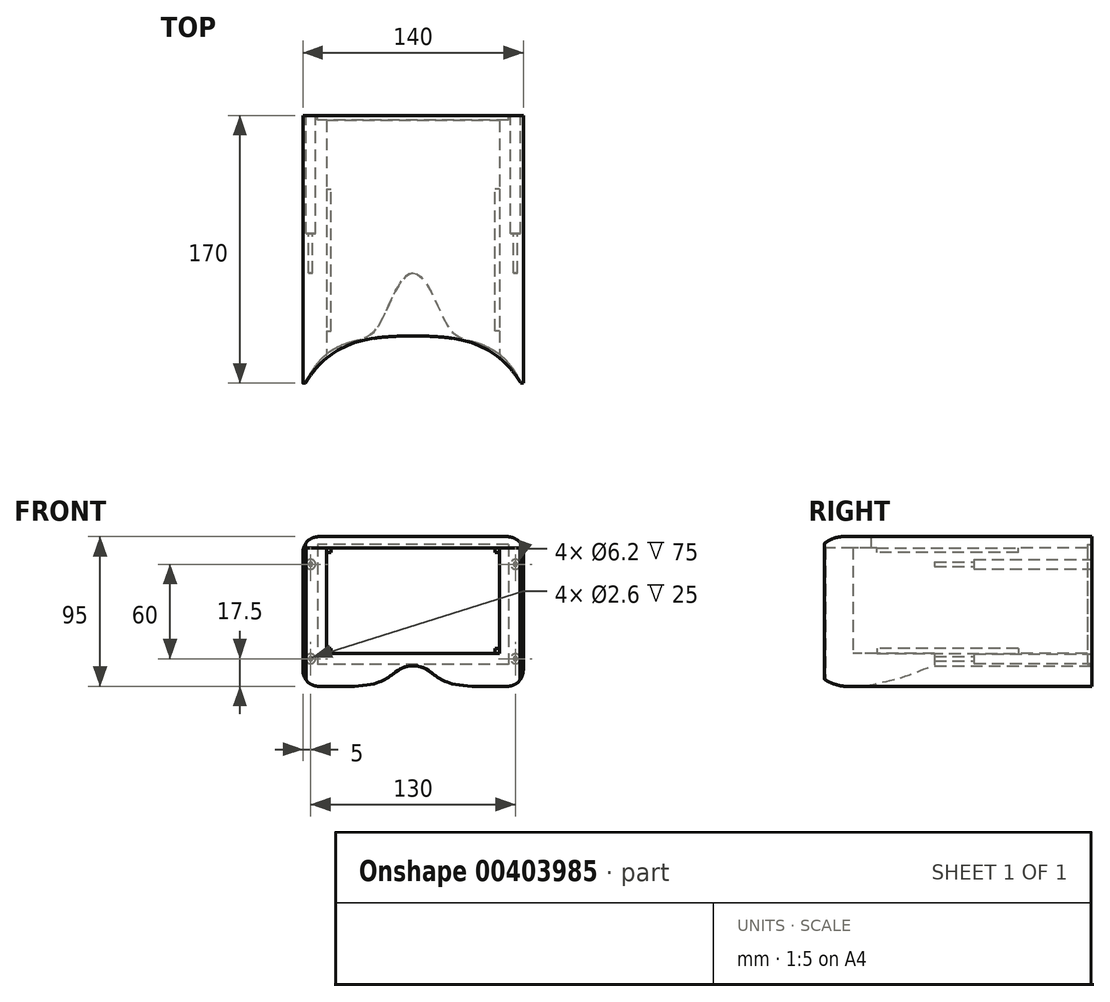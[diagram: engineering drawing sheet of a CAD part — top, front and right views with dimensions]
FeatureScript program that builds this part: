
annotation { "Feature Type Name" : "Feature", "Feature Type Description" : "" }
export const myFeature = defineFeature(function(context is Context, id is Id, definition is map)
    precondition{}
    {
        {
            var Q0;
            Q0=qCreatedBy(makeId("Top.planeOp"),FACE);
            var sketch = newSketch(context, id + "F0", { "sketchPlane" : qUnion([Q0])});
            skLineSegment(sketch, "E0.bottom", {"start": v(70, 85) * mm, "end": v(-70, 85) * mm});
            skLineSegment(sketch, "E0.top", {"start": v(70, -85) * mm, "end": v(-70, -85) * mm});
            skLineSegment(sketch, "E0.left", {"start": v(70, 85) * mm, "end": v(70, -85) * mm});
            skLineSegment(sketch, "E0.right", {"start": v(-70, 85) * mm, "end": v(-70, -85) * mm});
            skPoint(sketch, "E0.middle", {"position": v(0, 0) * mm});
            skSolve(sketch);
        }
        {
            var Q0;
            Q0=qSketchRegion(id+"F0",true);
            extrude(context, id + "F1", {"entities" : qUnion([Q0]), "depth" : 95 * mm});
        }
        {
            var Q0;
            Q0=makeQuery(id+"F1.opExtrude","SWEPT_FACE",FACE,{"disambiguationData":[OSD([sQuery(id+"F0.wireOp",EDGE,"E0.top")])]});
            var sketch = newSketch(context, id + "F2", { "sketchPlane" : qUnion([Q0])});
            skLineSegment(sketch, "E1.bottom", {"start": v(-55, 88) * mm, "end": v(55, 88) * mm});
            skLineSegment(sketch, "E1.top", {"start": v(-55, 21) * mm, "end": v(55, 21) * mm});
            skLineSegment(sketch, "E1.left", {"start": v(-55, 88) * mm, "end": v(-55, 21) * mm});
            skLineSegment(sketch, "E1.right", {"start": v(55, 88) * mm, "end": v(55, 21) * mm});
            skSolve(sketch);
        }
        {
            var Q0;
            Q0=qSketchRegion(id+"F2",true);
            extrude(context, id + "F3", {"entities" : qUnion([Q0]), "operationType" : NewBodyOperationType.REMOVE, "endBound" : BoundingType.THROUGH_ALL, "oppositeDirection" : true, "depth" : 25 * mm});
        }
        {
            var Q0;
            Q0=makeQuery(id+"F1.opExtrude","CAP_FACE",FACE,{"disambiguationData":[OSD([sQuery(id+"F0.wireOp",EDGE,"E0.bottom"),sQuery(id+"F0.wireOp",EDGE,"E0.top"),sQuery(id+"F0.wireOp",EDGE,"E0.left"),sQuery(id+"F0.wireOp",EDGE,"E0.right")])],"isStart":true});
            var sketch = newSketch(context, id + "F4", { "sketchPlane" : qUnion([Q0])});
            skLineSegment(sketch, "E2", {"start": v(0, -85) * mm, "end": v(0, 85) * mm, "construction": true});
            skLineSegment(sketch, "E3.1.0.0", {"start": v(-10, -85) * mm, "end": v(-10, 85) * mm, "construction": true});
            skLineSegment(sketch, "E3.2.0.0", {"start": v(-20, -85) * mm, "end": v(-20, 85) * mm, "construction": true});
            skLineSegment(sketch, "E3.3.0.0", {"start": v(-30, -85) * mm, "end": v(-30, 85) * mm, "construction": true});
            skLineSegment(sketch, "E3.4.0.0", {"start": v(-40, -85) * mm, "end": v(-40, 85) * mm, "construction": true});
            skLineSegment(sketch, "E3.5.0.0", {"start": v(-50, -85) * mm, "end": v(-50, 85) * mm, "construction": true});
            skLineSegment(sketch, "E3.6.0.0", {"start": v(-60, -85) * mm, "end": v(-60, 85) * mm, "construction": true});
            skLineSegment(sketch, "E3.direction1", {"start": v(0, -85) * mm, "end": v(-10, -85) * mm, "construction": true});
            skLineSegment(sketch, "E4.1.0.0", {"start": v(10, -85) * mm, "end": v(10, 85) * mm, "construction": true});
            skLineSegment(sketch, "E4.2.0.0", {"start": v(20, -85) * mm, "end": v(20, 85) * mm, "construction": true});
            skLineSegment(sketch, "E4.3.0.0", {"start": v(30, -85) * mm, "end": v(30, 85) * mm, "construction": true});
            skLineSegment(sketch, "E4.4.0.0", {"start": v(40, -85) * mm, "end": v(40, 85) * mm, "construction": true});
            skLineSegment(sketch, "E4.5.0.0", {"start": v(50, -85) * mm, "end": v(50, 85) * mm, "construction": true});
            skLineSegment(sketch, "E4.6.0.0", {"start": v(60, -85) * mm, "end": v(60, 85) * mm, "construction": true});
            skLineSegment(sketch, "E4.direction1", {"start": v(0, -85) * mm, "end": v(10, -85) * mm, "construction": true});
            skLineSegment(sketch, "E5", {"start": v(70, 15) * mm, "end": v(-70, 15) * mm, "construction": true});
            skLineSegment(sketch, "E6.0.1.0", {"start": v(70, 25) * mm, "end": v(-70, 25) * mm, "construction": true});
            skLineSegment(sketch, "E6.0.2.0", {"start": v(70, 35) * mm, "end": v(-70, 35) * mm, "construction": true});
            skLineSegment(sketch, "E6.0.3.0", {"start": v(70, 45) * mm, "end": v(-70, 45) * mm, "construction": true});
            skLineSegment(sketch, "E6.0.4.0", {"start": v(70, 55) * mm, "end": v(-70, 55) * mm, "construction": true});
            skLineSegment(sketch, "E6.0.5.0", {"start": v(70, 65) * mm, "end": v(-70, 65) * mm, "construction": true});
            skLineSegment(sketch, "E6.0.6.0", {"start": v(70, 75) * mm, "end": v(-70, 75) * mm, "construction": true});
            skLineSegment(sketch, "E6.1.0.0", {"start": v(95, 15) * mm, "end": v(-45, 15) * mm, "construction": true});
            skLineSegment(sketch, "E6.1.1.0", {"start": v(95, 25) * mm, "end": v(-45, 25) * mm, "construction": true});
            skLineSegment(sketch, "E6.1.2.0", {"start": v(95, 35) * mm, "end": v(-45, 35) * mm, "construction": true});
            skLineSegment(sketch, "E6.1.3.0", {"start": v(95, 45) * mm, "end": v(-45, 45) * mm, "construction": true});
            skLineSegment(sketch, "E6.1.4.0", {"start": v(95, 55) * mm, "end": v(-45, 55) * mm, "construction": true});
            skLineSegment(sketch, "E6.1.5.0", {"start": v(95, 65) * mm, "end": v(-45, 65) * mm, "construction": true});
            skLineSegment(sketch, "E6.1.6.0", {"start": v(95, 75) * mm, "end": v(-45, 75) * mm, "construction": true});
            skLineSegment(sketch, "E6.2.0.0", {"start": v(120, 15) * mm, "end": v(-20, 15) * mm, "construction": true});
            skLineSegment(sketch, "E6.2.1.0", {"start": v(120, 25) * mm, "end": v(-20, 25) * mm, "construction": true});
            skLineSegment(sketch, "E6.2.2.0", {"start": v(120, 35) * mm, "end": v(-20, 35) * mm, "construction": true});
            skLineSegment(sketch, "E6.2.3.0", {"start": v(120, 45) * mm, "end": v(-20, 45) * mm, "construction": true});
            skLineSegment(sketch, "E6.2.4.0", {"start": v(120, 55) * mm, "end": v(-20, 55) * mm, "construction": true});
            skLineSegment(sketch, "E6.2.5.0", {"start": v(120, 65) * mm, "end": v(-20, 65) * mm, "construction": true});
            skLineSegment(sketch, "E6.2.6.0", {"start": v(120, 75) * mm, "end": v(-20, 75) * mm, "construction": true});
            skLineSegment(sketch, "E6.direction1", {"start": v(-70, 15) * mm, "end": v(-45, 15) * mm, "construction": true});
            skLineSegment(sketch, "E6.direction2", {"start": v(-70, 15) * mm, "end": v(-70, 25) * mm, "construction": true});
            skFitSpline(sketch, "E7", {"points": [v(0, 15) * mm, v(20, 45) * mm, v(31.85, 56.6) * mm, v(68.26, 85) * mm], "startDerivative": vector(65.7, 0) * mm, "endDerivative": vector(77.5, 177.86) * mm});
            skFitSpline(sketch, "E8.MirrorCS", {"points": [v(0, 15) * mm, v(-20, 45) * mm, v(-31.85, 56.6) * mm, v(-68.26, 85) * mm], "startDerivative": vector(-65.7, 0) * mm, "endDerivative": vector(-77.5, 177.86) * mm});
            skLineSegment(sketch, "E9", {"start": v(68.26, 85) * mm, "end": v(-68.26, 85) * mm});
            skSolve(sketch);
        }
        {
            var Q0;
            Q0=makeQuery(id+"F4.imprint","IMPRINT",FACE,{"disambiguationData":[TD([[makeQuery(id+"F4.imprint","IMPRINT",EDGE,{"derivedFrom":sQuery(id+"F4.wireOp",EDGE,"E7")}),1.0]])]});
            extrude(context, id + "F5", {"entities" : qUnion([Q0]), "operationType" : NewBodyOperationType.REMOVE, "oppositeDirection" : true, "depth" : 88 * mm});
        }
        {
            var Q0;
            Q0=makeQuery(id+"F1.opExtrude","CAP_FACE",FACE,{"disambiguationData":[OSD([sQuery(id+"F0.wireOp",EDGE,"E0.bottom"),sQuery(id+"F0.wireOp",EDGE,"E0.top"),sQuery(id+"F0.wireOp",EDGE,"E0.left"),sQuery(id+"F0.wireOp",EDGE,"E0.right")])],"isStart":false});
            var sketch = newSketch(context, id + "F6", { "sketchPlane" : qUnion([Q0])});
            skLineSegment(sketch, "E10", {"start": v(-70, -55) * mm, "end": v(70, -55) * mm, "construction": true});
            skLineSegment(sketch, "E11", {"start": v(68.3, -85) * mm, "end": v(68.3, -55) * mm, "construction": true});
            skLineSegment(sketch, "E12", {"start": v(-68.36, -85) * mm, "end": v(-68.36, -55) * mm, "construction": true});
            skLineSegment(sketch, "E13", {"start": v(0, -85) * mm, "end": v(0, -55) * mm, "construction": true});
            skFitSpline(sketch, "E14", {"points": [v(0, -55) * mm, v(-47.97, -64.27) * mm, v(-68.36, -85) * mm], "startDerivative": vector(-134.93, 0) * mm, "endDerivative": vector(-37.97, -66.04) * mm});
            skFitSpline(sketch, "E15.MirrorCS", {"points": [v(0, -55) * mm, v(47.97, -64.27) * mm, v(68.36, -85) * mm], "startDerivative": vector(134.93, 0) * mm, "endDerivative": vector(37.97, -66.04) * mm});
            skLineSegment(sketch, "E16", {"start": v(-68.36, -85) * mm, "end": v(68.36, -85) * mm});
            skSolve(sketch);
        }
        {
            var Q0;
            Q0=makeQuery(id+"F6.imprint","IMPRINT",FACE,{"disambiguationData":[TD([[makeQuery(id+"F6.imprint","IMPRINT",EDGE,{"derivedFrom":sQuery(id+"F6.wireOp",EDGE,"E14")}),1.0]])]});
            extrude(context, id + "F7", {"entities" : qUnion([Q0]), "operationType" : NewBodyOperationType.REMOVE, "endBound" : BoundingType.UP_TO_NEXT, "oppositeDirection" : true, "depth" : 25 * mm});
        }
        {
            var Q0;
            Q0=makeQuery(id+"F1.opExtrude","CAP_EDGE",EDGE,{"disambiguationData":[OSD([sQuery(id+"F0.wireOp",EDGE,"E0.left")])],"isStart":false});
            var Q1;
            Q1=makeQuery(id+"F1.opExtrude","CAP_EDGE",EDGE,{"disambiguationData":[OSD([sQuery(id+"F0.wireOp",EDGE,"E0.left")])],"isStart":true});
            var Q2;
            Q2=makeQuery(id+"F1.opExtrude","CAP_EDGE",EDGE,{"disambiguationData":[OSD([sQuery(id+"F0.wireOp",EDGE,"E0.right")])],"isStart":true});
            var Q3;
            Q3=makeQuery(id+"F1.opExtrude","CAP_EDGE",EDGE,{"disambiguationData":[OSD([sQuery(id+"F0.wireOp",EDGE,"E0.right")])],"isStart":false});
            fillet(context, id + "F8", {"entities" : qUnion([Q0, Q1, Q2, Q3]), "radius" : 10 * mm, "tangentPropagation" : true, "allowEdgeOverflow" : false});
        }
        {
            var Q0;
            Q0=makeQuery(id+"F1.opExtrude","SWEPT_FACE",FACE,{"disambiguationData":[OSD([sQuery(id+"F0.wireOp",EDGE,"E0.bottom")])]});
            var sketch = newSketch(context, id + "F9", { "sketchPlane" : qUnion([Q0])});
            skLineSegment(sketch, "E17", {"start": v(0, 21) * mm, "end": v(0, 0) * mm, "construction": true});
            skLineSegment(sketch, "E18", {"start": v(-70, 13) * mm, "end": v(70, 13) * mm, "construction": true});
            skLineSegment(sketch, "E19", {"start": v(-40, 21) * mm, "end": v(-40, 0) * mm, "construction": true});
            skFitSpline(sketch, "E20", {"points": [v(0, 13) * mm, v(-40, 0) * mm], "startDerivative": vector(-42.54, 0) * mm, "endDerivative": vector(-86.95, 0) * mm});
            skFitSpline(sketch, "E21.MirrorCS", {"points": [v(0, 13) * mm, v(40, 0) * mm], "startDerivative": vector(42.54, 0) * mm, "endDerivative": vector(86.95, 0) * mm});
            skLineSegment(sketch, "E22", {"start": v(40, 0) * mm, "end": v(-40, 0) * mm});
            skSolve(sketch);
        }
        {
            var Q0;
            Q0=makeQuery(id+"F9.imprint","IMPRINT",FACE,{"disambiguationData":[TD([[makeQuery(id+"F9.imprint","IMPRINT",EDGE,{"derivedFrom":sQuery(id+"F9.wireOp",EDGE,"E20")}),1.0]])]});
            extrude(context, id + "F10", {"entities" : qUnion([Q0]), "operationType" : NewBodyOperationType.REMOVE, "endBound" : BoundingType.THROUGH_ALL, "oppositeDirection" : true, "depth" : 25 * mm});
        }
        {
            var Q0;
            Q0=makeQuery(id+"F1.opExtrude","SWEPT_FACE",FACE,{"disambiguationData":[OSD([sQuery(id+"F0.wireOp",EDGE,"E0.bottom")])]});
            var sketch = newSketch(context, id + "F11", { "sketchPlane" : qUnion([Q0])});
            skLineSegment(sketch, "E23.bottom", {"start": v(-60.5, 90) * mm, "end": v(60.5, 90) * mm});
            skLineSegment(sketch, "E23.top", {"start": v(-60.5, 14) * mm, "end": v(60.5, 14) * mm});
            skLineSegment(sketch, "E23.left", {"start": v(-60.5, 90) * mm, "end": v(-60.5, 14) * mm});
            skLineSegment(sketch, "E23.right", {"start": v(60.5, 90) * mm, "end": v(60.5, 14) * mm});
            skSolve(sketch);
        }
        {
            var Q0;
            Q0=makeQuery(id+"F11.imprint","IMPRINT",FACE,{"disambiguationData":[TD([[makeQuery(id+"F11.imprint","IMPRINT",EDGE,{"derivedFrom":sQuery(id+"F11.wireOp",EDGE,"E23.bottom")}),-1.0]])]});
            extrude(context, id + "F12", {"entities" : qUnion([Q0]), "operationType" : NewBodyOperationType.REMOVE, "oppositeDirection" : true, "depth" : 3 * mm});
        }
        {
            var Q0;
            Q0=makeQuery(id+"F3.boolean.opBoolean","COPY",FACE,{"derivedFrom":makeQuery(id+"F3.opExtrude","SWEPT_FACE",FACE,{"disambiguationData":[OSD([sQuery(id+"F2.wireOp",EDGE,"E1.top")])]})});
            var sketch = newSketch(context, id + "F13", { "sketchPlane" : qUnion([Q0])});
            skLineSegment(sketch, "E24.bottom", {"start": v(-55, -51.7) * mm, "end": v(-52, -51.7) * mm});
            skLineSegment(sketch, "E24.top", {"start": v(-55, 38.3) * mm, "end": v(-52, 38.3) * mm});
            skLineSegment(sketch, "E24.left", {"start": v(-55, -51.7) * mm, "end": v(-55, 38.3) * mm});
            skLineSegment(sketch, "E24.right", {"start": v(-52, -51.7) * mm, "end": v(-52, 38.3) * mm});
            skLineSegment(sketch, "E25.bottom", {"start": v(55, -51.7) * mm, "end": v(52, -51.7) * mm});
            skLineSegment(sketch, "E25.top", {"start": v(55, 38.3) * mm, "end": v(52, 38.3) * mm});
            skLineSegment(sketch, "E25.left", {"start": v(55, -51.7) * mm, "end": v(55, 38.3) * mm});
            skLineSegment(sketch, "E25.right", {"start": v(52, -51.7) * mm, "end": v(52, 38.3) * mm});
            skSolve(sketch);
        }
        {
            var Q0;
            Q0=qSketchRegion(id+"F13",true);
            extrude(context, id + "F14", {"entities" : qUnion([Q0]), "operationType" : NewBodyOperationType.ADD, "depth" : 3 * mm});
        }
        {
            var Q0;
            Q0=makeQuery(id+"F5.boolean.opBoolean","MERGE",FACE,{"derivedFrom":[makeQuery(id+"F3.boolean.opBoolean","COPY",FACE,{"derivedFrom":makeQuery(id+"F3.opExtrude","SWEPT_FACE",FACE,{"disambiguationData":[OSD([sQuery(id+"F2.wireOp",EDGE,"E1.bottom")])]})}),makeQuery(id+"F5.opExtrude","CAP_FACE",FACE,{"disambiguationData":[OSD([sQuery(id+"F4.wireOp",EDGE,"E7"),sQuery(id+"F4.wireOp",EDGE,"E8.MirrorCS"),sQuery(id+"F4.wireOp",EDGE,"E9")])],"isStart":false})]});
            var sketch = newSketch(context, id + "F15", { "sketchPlane" : qUnion([Q0])});
            skLineSegment(sketch, "E26.bottom", {"start": v(55, 51.7) * mm, "end": v(52, 51.7) * mm});
            skLineSegment(sketch, "E26.top", {"start": v(55, -38.3) * mm, "end": v(52, -38.3) * mm});
            skLineSegment(sketch, "E26.left", {"start": v(55, 51.7) * mm, "end": v(55, -38.3) * mm});
            skLineSegment(sketch, "E26.right", {"start": v(52, 51.7) * mm, "end": v(52, -38.3) * mm});
            skLineSegment(sketch, "E27.bottom", {"start": v(-55, 51.7) * mm, "end": v(-52, 51.7) * mm});
            skLineSegment(sketch, "E27.top", {"start": v(-55, -38.3) * mm, "end": v(-52, -38.3) * mm});
            skLineSegment(sketch, "E27.left", {"start": v(-55, 51.7) * mm, "end": v(-55, -38.3) * mm});
            skLineSegment(sketch, "E27.right", {"start": v(-52, 51.7) * mm, "end": v(-52, -38.3) * mm});
            skSolve(sketch);
        }
        {
            var Q0;
            Q0=qSketchRegion(id+"F15",true);
            extrude(context, id + "F16", {"entities" : qUnion([Q0]), "operationType" : NewBodyOperationType.ADD, "depth" : 3 * mm});
        }
        {
            var Q0;
            Q0=makeQuery(id+"F1.opExtrude","SWEPT_FACE",FACE,{"disambiguationData":[OSD([sQuery(id+"F0.wireOp",EDGE,"E0.bottom")])]});
            var sketch = newSketch(context, id + "F17", { "sketchPlane" : qUnion([Q0])});
            skLineSegment(sketch, "E28", {"start": v(-70, 47.5) * mm, "end": v(70, 47.5) * mm, "construction": true});
            skCircle(sketch, "E29", {"center": v(65, 77.5) * mm, "radius": 1.3 * mm});
            skLineSegment(sketch, "E30", {"start": v(0, 95) * mm, "end": v(0, 13) * mm, "construction": true});
            skCircle(sketch, "E31.MirrorC", {"center": v(65, 17.5) * mm, "radius": 1.3 * mm});
            skCircle(sketch, "E32.MirrorC", {"center": v(-65, 77.5) * mm, "radius": 1.3 * mm});
            skCircle(sketch, "E33.MirrorC", {"center": v(-65, 17.5) * mm, "radius": 1.3 * mm});
            skSolve(sketch);
        }
        {
            var Q0;
            Q0 = qSketchRegion(id + "F17", true);
            extrude(context, id + "F18", {"entities" : qUnion([Q0]), "operationType" : NewBodyOperationType.REMOVE, "oppositeDirection" : true, "depth" : 100 * mm});
        }
        {
            var Q0;
            Q0=makeQuery(id+"F17.imprint","IMPRINT",FACE,{"disambiguationData":[TD([[makeQuery(id+"F17.imprint","IMPRINT",EDGE,{"derivedFrom":sQuery(id+"F17.wireOp",EDGE,"E29")}),-1.0]])]});
            var sketch = newSketch(context, id + "F19", { "sketchPlane" : qUnion([Q0])});
            skCircle(sketch, "E34", {"center": v(65, 77.5) * mm, "radius": 3.1 * mm});
            skCircle(sketch, "E35.MirrorC", {"center": v(65, 17.5) * mm, "radius": 3.1 * mm});
            skCircle(sketch, "E36.MirrorC", {"center": v(-65, 77.5) * mm, "radius": 3.1 * mm});
            skCircle(sketch, "E37.MirrorC", {"center": v(-65, 17.5) * mm, "radius": 3.1 * mm});
            skSolve(sketch);
        }
        {
            var Q0;
            Q0 = qSketchRegion(id + "F19", true);
            extrude(context, id + "F20", {"entities" : qUnion([Q0]), "operationType" : NewBodyOperationType.REMOVE, "oppositeDirection" : true, "depth" : 75 * mm});
        }
    });
